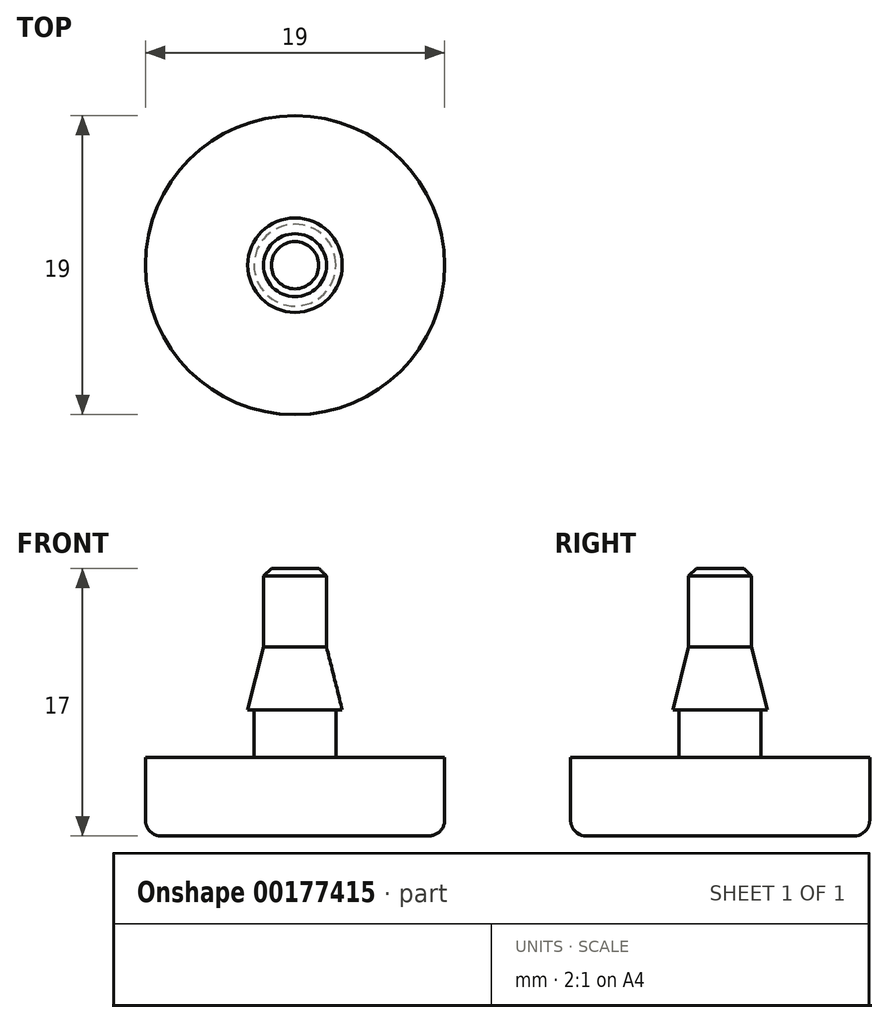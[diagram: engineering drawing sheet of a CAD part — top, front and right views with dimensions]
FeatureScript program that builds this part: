
annotation { "Feature Type Name" : "Feature", "Feature Type Description" : "" }
export const myFeature = defineFeature(function(context is Context, id is Id, definition is map)
    precondition{}
    {
        {
            var Q0;
            Q0=qCreatedBy(makeId("Top.planeOp"),FACE);
            var sketch = newSketch(context, id + "F0", { "sketchPlane" : qUnion([Q0])});
            skCircle(sketch, "E0", {"center": v(0, 0) * mm, "radius": 9.5 * mm});
            skSolve(sketch);
        }
        {
            var Q0;
            Q0 = qSketchRegion(id + "F0", true);
            extrude(context, id + "F1", {"entities" : qUnion([Q0]), "depth" : 5 * mm});
        }
        {
            var Q0;
            Q0=makeQuery(id+"F1.opExtrude","CAP_EDGE",EDGE,{"disambiguationData":[OSD([sQuery(id+"F0.wireOp",EDGE,"E0")])],"isStart":true});
            fillet(context, id + "F2", {"entities" : qUnion([Q0]), "radius" : 1 * mm, "tangentPropagation" : true, "allowEdgeOverflow" : false});
        }
        {
            var Q0;
            Q0=makeQuery(id+"F1.opExtrude","CAP_FACE",FACE,{"disambiguationData":[OSD([sQuery(id+"F0.wireOp",EDGE,"E0")])],"isStart":false});
            cPlane(context, id + "F3", {"entities" : qUnion([Q0]), "cplaneType" : CPlaneType.OFFSET, "offset" : 3 * mm, "width" : 150 * mm, "height" : 150 * mm});
        }
        {
            var Q0;
            Q0=qCreatedBy(id+"F3.planeOp",FACE);
            var sketch = newSketch(context, id + "F4", { "sketchPlane" : qUnion([Q0])});
            skCircle(sketch, "E1", {"center": v(0, 0) * mm, "radius": 3 * mm});
            skSolve(sketch);
        }
        {
            var Q0;
            Q0=qCreatedBy(id+"F3.planeOp",FACE);
            cPlane(context, id + "F5", {"entities" : qUnion([Q0]), "cplaneType" : CPlaneType.OFFSET, "offset" : 4 * mm, "width" : 150 * mm, "height" : 150 * mm});
        }
        {
            var Q0;
            Q0=qCreatedBy(id+"F5.planeOp",FACE);
            var sketch = newSketch(context, id + "F6", { "sketchPlane" : qUnion([Q0])});
            skCircle(sketch, "E2", {"center": v(0, 0) * mm, "radius": 2 * mm});
            skSolve(sketch);
        }
        {
            var Q0;
            Q0=makeQuery(id+"F4.imprint","IMPRINT",FACE,{"disambiguationData":[TD([[makeQuery(id+"F4.imprint","IMPRINT",EDGE,{"derivedFrom":sQuery(id+"F4.wireOp",EDGE,"E1")}),1.0]])]});
            var Q1;
            Q1=makeQuery(id+"F6.imprint","IMPRINT",FACE,{"disambiguationData":[TD([[makeQuery(id+"F6.imprint","IMPRINT",EDGE,{"derivedFrom":sQuery(id+"F6.wireOp",EDGE,"E2")}),1.0]])]});
            loft(context, id + "F7", {"sheetProfilesArray" : [{ "sheetProfileEntities" : qUnion([Q0]) }, { "sheetProfileEntities" : qUnion([Q1]) }]});
        }
        {
            var Q0;
            Q0=makeQuery(id+"F1.opExtrude","CAP_FACE",FACE,{"disambiguationData":[OSD([sQuery(id+"F0.wireOp",EDGE,"E0")])],"isStart":false});
            var sketch = newSketch(context, id + "F8", { "sketchPlane" : qUnion([Q0])});
            skCircle(sketch, "E3", {"center": v(0, 0) * mm, "radius": 2.6 * mm});
            skSolve(sketch);
        }
        {
            var Q0;
            Q0=makeQuery(id+"F8.imprint","IMPRINT",FACE,{"disambiguationData":[TD([[makeQuery(id+"F8.imprint","IMPRINT",EDGE,{"derivedFrom":sQuery(id+"F8.wireOp",EDGE,"E3")}),1.0]])]});
            extrude(context, id + "F9", {"entities" : qUnion([Q0]), "operationType" : NewBodyOperationType.ADD, "depth" : 3 * mm});
        }
        {
            var Q0;
            Q0=makeQuery(id+"F7.opLoft","CAP_FACE",FACE,{"disambiguationData":[OSD([makeQuery(id+"F6.imprint","IMPRINT",FACE,{"disambiguationData":[TD([[makeQuery(id+"F6.imprint","IMPRINT",EDGE,{"derivedFrom":sQuery(id+"F6.wireOp",EDGE,"E2")}),1.0]])]})])],"isStart":true});
            extrude(context, id + "F10", {"entities" : qUnion([Q0]), "operationType" : NewBodyOperationType.ADD, "depth" : 5 * mm});
        }
        {
            var Q0;
            Q0=makeQuery(id+"F10.opExtrude","CAP_EDGE",EDGE,{"disambiguationData":[OSD([sQuery(id+"F4.wireOp",EDGE,"E1"),sQuery(id+"F6.wireOp",EDGE,"E2")])],"isStart":false});
            chamfer(context, id + "F11", {"entities" : qUnion([Q0]), "width" : .5 * mm, "tangentPropagation" : true});
        }
    });
